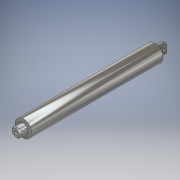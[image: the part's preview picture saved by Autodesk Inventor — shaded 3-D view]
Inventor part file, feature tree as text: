
AUTODESK INVENTOR PART (.ipt)
format: ipt  version: 2017 SP1 (Build 210196100, 196)  size: 131,584 bytes
history: native  units: in
note: dims shown in document units (in); Inventor stores cm internally (conversion verified against a paired STEP export)
features: extrude x5, sketch x5, chamfer x1
ambient origin geometry x8: Origin, YZ Plane, XZ Plane, XY Plane, X Axis, Y Axis, Z Axis, Center Point
bodies: Solid1 (feature_tree)
feature tree (11):
  extrude  "Extrusion1"  Depth=8.75in TaperAngle=0.0deg
  extrude  "Extrusion2"  Depth=0.3125in
  extrude  "Extrusion3"  Depth=0.625in
  extrude  "Extrusion4"  Depth=0.625in TaperAngle=0.0deg
  chamfer  "Chamfer1"  Distance=0.5in
  extrude  "Extrusion5"  Depth=0.125in TaperAngle=45.0deg
  sketch  "Sketch1"  dims[d0=1.118in d1=8.75in d2=0.0in]
  sketch  "Sketch2"  dims[d3=0.375in d4=0.3125in]
  sketch  "Sketch3"  dims[d5=0.625in d6=0.0in d7=0.26in]
  sketch  "Sketch4"  dims[d8=0.25in d9=0.625in d10=0.0in]
  sketch  "Sketch5"  dims[d11=0.625in d12=0.5in d13=0.0in d14=0.0625in d15=0.125in d16=45.0deg d17=0.25in d18=6.0in d19=0.0in]
